# Revit family: HVAC_HangingSystems_Walraven_BIS_Strut_Rail_End_Cap
name_source: partatom
category: Mechanical Equipment
revit_build: Autodesk Revit MEP 2016 (Build: 20150220_1215(x64)
units: mm (PartAtom-declared; Revit-internal decimal feet)

## family parameters
Always vertical = No
Cut with Voids When Loaded = No
OmniClass Number = 23.60.30.11.17
OmniClass Title = Pipework/Ductwork Mechanical Fasteners/Supports
Part Type = Normal
Room Calculation Point = No
Round Connector Dimension = Use Diameter
Shared = No
Work Plane-Based = Yes

## types (5) — shared parameters
BIMobject category = Hanging Systems
BIMobject category code = hvac-hanging-systems
BIMobject main category = HVAC
BIMobject main category code = hvac
Brand url = https://www.walraven.com
Date of publishing = 7/20/2018
Default Elevation = 1219 mm
Description = rail end cap
Design country = Netherlands
IFC Classification = Mechanical Fastener
IfcDescription = rail end cap
IfcExportAs = IfcMechanicalFastenerType
IfcExportType = USERDEFINED
Manufacturer = Walraven
Manufacturer country = Netherlands
Manufacturer name = Walraven
Material main = Polyethylene
Model = BIS Strut Rail End Cap
NLRS_C_code_SfB_tabel1 = 50
Nominal width = 41 mm  [stored 0.134514 ft]
OmniClass Code = 23-27 43 13
OmniClass Description = Mechanical Pipe Supports
Product Guid = cc4c4626-3c83-4a75-b29f-4aced200335d
Product SKU = bis-strut-rail-end-cap
Product data url = https://bimobject.com
Product family = Rail Systems
Product group = End Caps
Product url = https://www.walraven.com
QR code = http://bimobject.com
RSen_C_code_ETIM = EC000475
RSen_C_code_ETIM_url = https://prod.etim-international.com
RSen_C_content_modification_date = 04-06-2018
RSen_C_content_releasedate = 22-02-2018
RSen_C_intended_use = hanging systems
RSen_C_level_of_development = LOD400
RSen_C_material = polyethylene (PE)
RSen_C_material_colour = green
Technical description = https://library.walraven.com
URL = https://www.walraven.com
region_index = 1
zero-valued in all types: Edition number, Nominal height

## per-type parameters (varying)
| type | Assembly Code | type_index |
| 41x51 (DS 5) |  | 3 |
| 41x41 | 50 | 2 |
| 41x21 | 50 | 1 |
| 41x62 | 50 | 4 |
| 41x82 | 50 | 5 |

note: [stored X ft] marks values corroborated as IEEE doubles in the binary element streams (Revit-internal decimal feet)

## geometry (parser evidence)
native form markers: Blend x2, Sweep x3
no freeform markers — native parametric forms only
